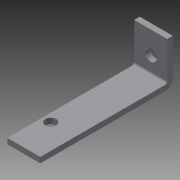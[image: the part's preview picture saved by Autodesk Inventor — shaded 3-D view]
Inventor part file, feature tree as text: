
AUTODESK INVENTOR PART (.ipt)
format: ipt  version: 2013 (Build 170138000, 138)  size: 211,456 bytes
history: native  units: in
note: dims shown in document units (in); Inventor stores cm internally (conversion verified against a paired STEP export)
features: sketch x11, sheet_metal_op x10, other x7, extrude x5, reference x1
ambient origin geometry x8: Origin, YZ Plane, XZ Plane, XY Plane, X Axis, Y Axis, Z Axis, Center Point
bodies: Solid1 (feature_tree)
feature tree (34):
  sheet_metal_op  "Face1"
  sheet_metal_op  "Flange1"
  extrude  "Extrusion1"  Depth=0.125in
  sketch  "Sketch7"  dims[d10=0.125in d11=2.0in d12=0.0in]
  sketch  "Sketch8"  dims[d19=1.3125in]
  sketch  "Sketch9"  dims[d20=2.1in]
  extrude  "Extrusion4"  Depth=0.25in
  extrude  "Extrusion5"  Depth=1.0in TaperAngle=90.0deg
  extrude  "Extrusion6"  Depth=0.125in
  extrude  "Extrusion7"  Depth=2.0in TaperAngle=0.0deg
  sheet_metal_op  "Flange2"
  sheet_metal_op  "Flange3"
  sketch  "Sketch1"  dims[d0=0.125in d1=0.125in]
  other  "Plate1"
  sketch  "Sketch2"  dims[d2=0.0625in d3=0.25in]
  other  "Plate2"
  sheet_metal_op  "Bend1"
  sheet_metal_op  "Corner1"
  sketch  "Sketch3"  dims[d4=0.125in d5=1.0in d6=90.0deg d7=0.05in]
  sketch  "Sketch6"  dims[d8=0.5in d9=0.125in]
  reference  "Reference1"
  sketch  "Sketch10"  dims[d21=0.25in]
  sketch  "Sketch11"  dims[d22=0.125in]
  other  "Plate3"
  sheet_metal_op  "Bend2"
  sheet_metal_op  "Corner2"
  sketch  "Sketch12"  dims[d23=0.0in]
  other  "Plate4"
  sheet_metal_op  "Bend3"
  sheet_metal_op  "Corner3"
  sketch  "Sketch13"  dims[d24=0.125in d25=0.0in d26=0.125in d27=0.0in d28=0.125in d29=0.0in d30=0.5in d31=0.0in d32=0.125in d33=0.0625in d34=0.25in d35=0.125in d36=1.0in d37=90.0deg d38=0.05in d39=0.5in d40=0.125in d41=0.125in d42=0.125in d43=0.0625in d44=0.25in d45=0.125in d46=1.0in d47=90.0deg d48=0.05in d49=0.5in d50=0.125in d51=0.125in d52=0.125in d53=0.0in]
  other  "Cut1"
  other  "Cut2"
  other  "Definition1"
